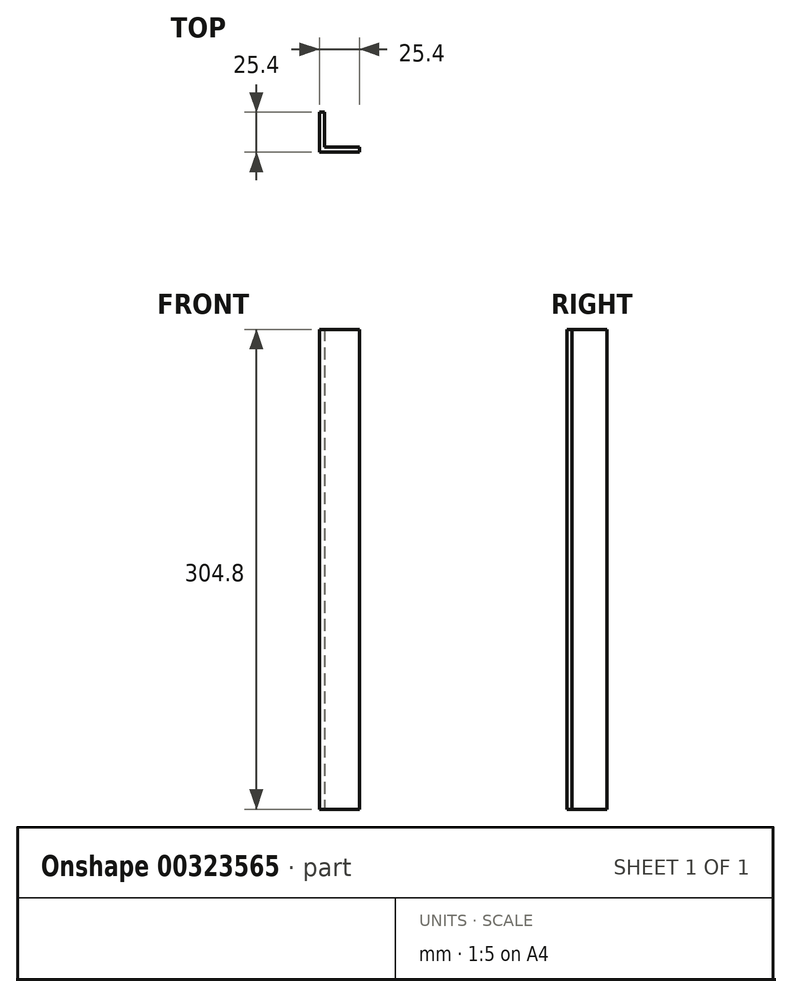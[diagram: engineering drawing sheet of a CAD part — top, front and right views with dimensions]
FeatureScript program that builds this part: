
annotation { "Feature Type Name" : "Feature", "Feature Type Description" : "" }
export const myFeature = defineFeature(function(context is Context, id is Id, definition is map)
    precondition{}
    {
        {
            var Q0;
            Q0=qCreatedBy(makeId("Top.planeOp"),FACE);
            var sketch = newSketch(context, id + "F0", { "sketchPlane" : qUnion([Q0])});
            skLineSegment(sketch, "E0.bottom", {"start": v(1.59, 12.7) * mm, "end": v(-1.59, 12.7) * mm});
            skLineSegment(sketch, "E0.top", {"start": v(1.59, -12.7) * mm, "end": v(-1.59, -12.7) * mm});
            skLineSegment(sketch, "E0.left", {"start": v(1.59, 12.7) * mm, "end": v(1.59, -12.7) * mm});
            skLineSegment(sketch, "E0.right", {"start": v(-1.59, 12.7) * mm, "end": v(-1.59, -12.7) * mm});
            skPoint(sketch, "E0.middle", {"position": v(0, 0) * mm});
            skLineSegment(sketch, "E1.left", {"start": v(1.59, -12.7) * mm, "end": v(1.59, 0) * mm});
            skLineSegment(sketch, "E2.bottom", {"start": v(1.59, -12.7) * mm, "end": v(23.81, -12.7) * mm});
            skLineSegment(sketch, "E2.top", {"start": v(1.59, -9.53) * mm, "end": v(23.81, -9.53) * mm});
            skLineSegment(sketch, "E2.left", {"start": v(1.59, -12.7) * mm, "end": v(1.59, -9.53) * mm});
            skLineSegment(sketch, "E2.right", {"start": v(23.81, -12.7) * mm, "end": v(23.81, -9.53) * mm});
            skSolve(sketch);
        }
        {
            var Q0;
            Q0=makeQuery(id+"F0.imprint","IMPRINT",FACE,{"disambiguationData":[TD([[makeQuery(id+"F0.imprint","IMPRINT",EDGE,{"derivedFrom":sQuery(id+"F0.wireOp",EDGE,"E0.bottom")}),1.0]])]});
            var Q1;
            Q1=makeQuery(id+"F0.imprint","IMPRINT",FACE,{"disambiguationData":[TD([[makeQuery(id+"F0.imprint","IMPRINT",EDGE,{"derivedFrom":sQuery(id+"F0.wireOp",EDGE,"E2.bottom")}),1.0]])]});
            extrude(context, id + "F1", {"entities" : qUnion([Q0, Q1]), "depth" : 304.8 * mm});
        }
    });
